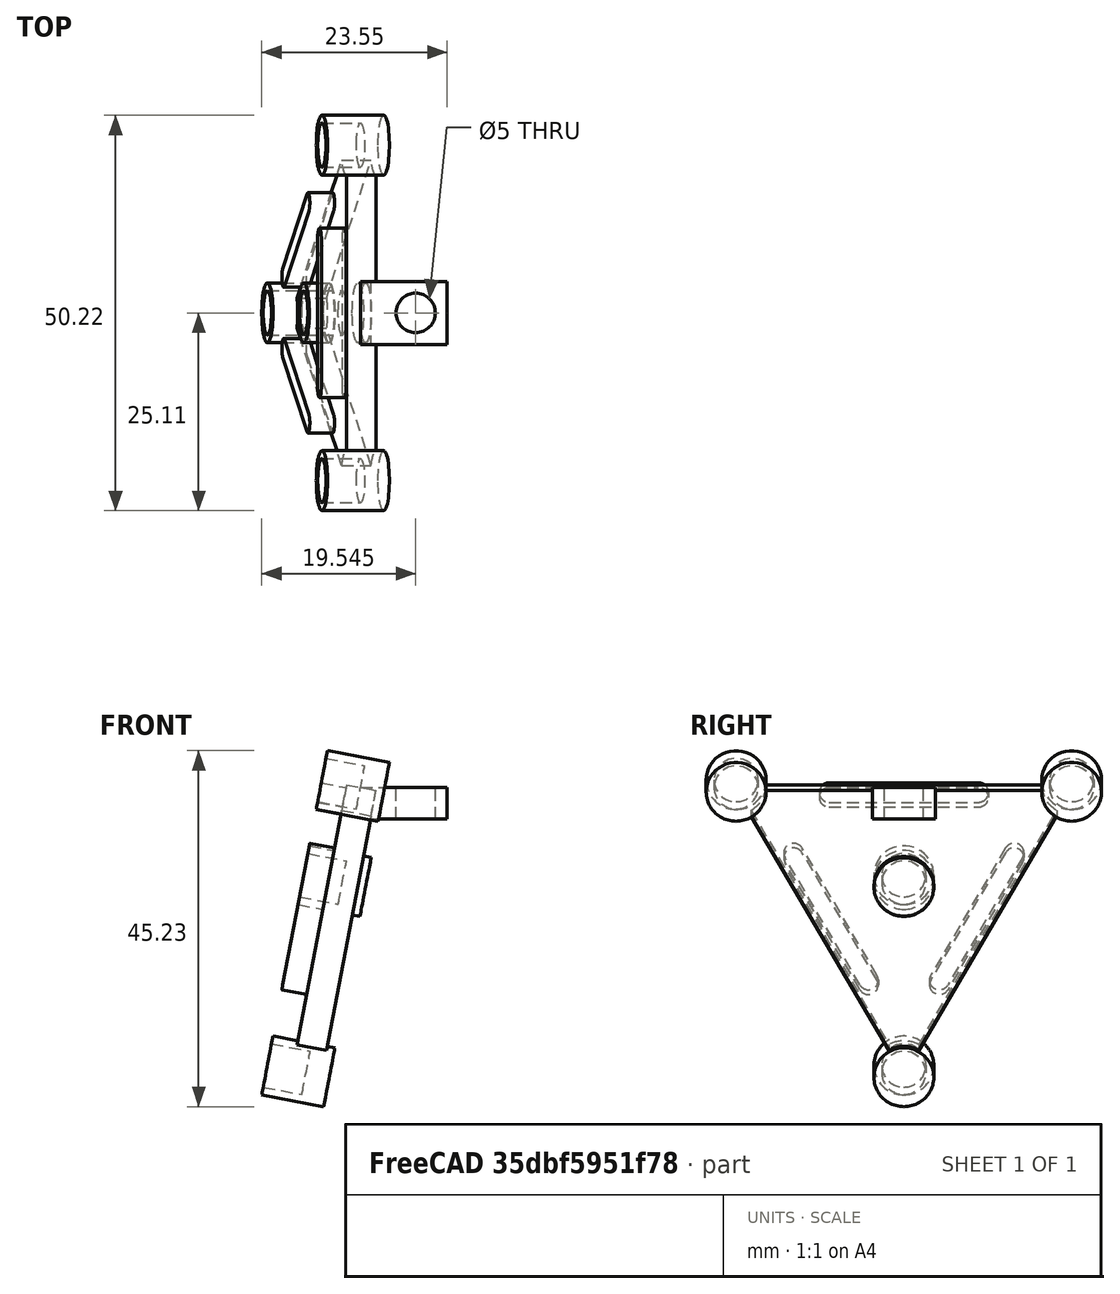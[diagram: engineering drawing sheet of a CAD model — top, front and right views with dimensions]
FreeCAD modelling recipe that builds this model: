
FCSTD DOCUMENT  (FreeCAD 0.19R24267 +99 (Git))
Label: PCB_export
License: All rights reserved
LicenseURL: http://en.wikipedia.org/wiki/All_rights_reserved
objects: Part::Feature×3, Part::Part2DObjectPython×2, Sketcher::SketchObject×2
note: 7 computed .brp shape members not serialized (recipe doc carries the construction recipe); baked Part::Feature solids carry a one-line shape summary decoded from their .brp

FEATURE [Part::Feature] Shape
  Placement = pos=(0,0,0) rot=(0,1,0;0.188711rad)
  shape: bbox 26.49 x 83.96 x 75.99 mm, 229 faces (baked)
FEATURE [Part::Feature] Shape001
  Placement = pos=(0,0,0) rot=(0,1,0;0.188711rad)
  shape: bbox 11.8 x 62.95 x 53.85 mm, 54 faces (baked)
FEATURE [Part::Feature] Shape002
  shape: bbox 23.55 x 50.22 x 45.22 mm, 59 faces (baked)
FEATURE [Part::Part2DObjectPython] Shape2DView  # Draft 2D object (typed FeaturePython)
  Base = -> Shape
  FuseArch = false
  HiddenLines = false
  InPlace = true
  Projection = (0.982247,0,-0.187593)
  ProjectionMode = 0
  SegmentLength = 0.05
  Tessellation = false
  VisibleOnly = false
FEATURE [Part::Part2DObjectPython] Shape2DView001  # Draft 2D object (typed FeaturePython)
  Base = -> Shape001
  FuseArch = false
  HiddenLines = false
  InPlace = true
  Projection = (0.982247,0,-0.187593)
  ProjectionMode = 0
  SegmentLength = 0.05
  Tessellation = false
  VisibleOnly = false
FEATURE [Sketcher::SketchObject] Sketch  label="pcb_all"
  ExternalGeometry = -> [Shape2DView001]
  FullyConstrained = false
  Placement = pos=(0,0,0) rot=(0,0,1;3.14159rad)
  sketch-geometry (323):
    g0: ArcOfEllipse CenterX=-1.99e-14 CenterY=3.45e-14 CenterZ=0 NormalX=0 NormalY=0 NormalZ=1 MajorRadius=76.0845 MinorRadius=27.1486 AngleXU=0.523599 StartAngle=4.15881 EndAngle=5.26596
    g1: ArcOfEllipse CenterX=0 CenterY=0 CenterZ=0 NormalX=0 NormalY=0 NormalZ=1 MajorRadius=76.0845 MinorRadius=27.1486 AngleXU=2.61799 StartAngle=4.15881 EndAngle=5.26596
    g2: ArcOfEllipse CenterX=0 CenterY=0 CenterZ=0 NormalX=0 NormalY=0 NormalZ=1 MajorRadius=76.0845 MinorRadius=27.1486 AngleXU=-1.5708 StartAngle=4.15881 EndAngle=5.26596
    g3: LineSegment StartX=-20.8022 StartY=-36.0305 StartZ=0 EndX=-23.094 EndY=-40 EndZ=0
    g4: LineSegment StartX=41.6044 StartY=-5.68e-14 StartZ=0 EndX=-20.8022 EndY=-36.0305 EndZ=0
    g5: LineSegment StartX=41.6044 StartY=-4.77e-14 StartZ=0 EndX=46.188 EndY=-4.83e-14 EndZ=0
    g6: ArcOfEllipse CenterX=1.78111 CenterY=-28.2981 CenterZ=0 NormalX=0 NormalY=0 NormalZ=1 MajorRadius=2.8 MinorRadius=0.999102 AngleXU=0.523599 StartAngle=3.14159 EndAngle=4.71239
    g7: ArcOfEllipse CenterX=1.78111 CenterY=-28.2981 CenterZ=0 NormalX=0 NormalY=0 NormalZ=1 MajorRadius=2.8 MinorRadius=0.999102 AngleXU=0.523599 StartAngle=0 EndAngle=3.14159
    g8: ArcOfEllipse CenterX=1.78111 CenterY=-28.2981 CenterZ=0 NormalX=0 NormalY=0 NormalZ=1 MajorRadius=2.8 MinorRadius=0.999102 AngleXU=0.523599 StartAngle=4.71239 EndAngle=6.28319
    g9: ArcOfEllipse CenterX=12.8964 CenterY=-22.3371 CenterZ=0 NormalX=0 NormalY=0 NormalZ=1 MajorRadius=2.8 MinorRadius=0.999102 AngleXU=0.523599 StartAngle=3.14159 EndAngle=4.71239
    g10: ArcOfEllipse CenterX=12.8964 CenterY=-22.3371 CenterZ=0 NormalX=0 NormalY=0 NormalZ=1 MajorRadius=2.8 MinorRadius=0.999102 AngleXU=0.523599 StartAngle=1.42745 EndAngle=3.14159
    g11: ArcOfEllipse CenterX=12.8964 CenterY=-22.3371 CenterZ=0 NormalX=0 NormalY=0 NormalZ=1 MajorRadius=2.8 MinorRadius=0.999102 AngleXU=0.523599 StartAngle=0 EndAngle=0.600419
    g12: ArcOfEllipse CenterX=12.8964 CenterY=-22.3371 CenterZ=0 NormalX=0 NormalY=0 NormalZ=1 MajorRadius=2.8 MinorRadius=0.999102 AngleXU=0.523599 StartAngle=4.71239 EndAngle=6.28319
    g13: ArcOfEllipse CenterX=-9.38874 CenterY=-33.3917 CenterZ=0 NormalX=0 NormalY=0 NormalZ=1 MajorRadius=2.8 MinorRadius=0.999102 AngleXU=0.523599 StartAngle=3.14159 EndAngle=4.71239
    g14: ArcOfEllipse CenterX=-9.38874 CenterY=-33.3917 CenterZ=0 NormalX=0 NormalY=0 NormalZ=1 MajorRadius=2.8 MinorRadius=0.999102 AngleXU=0.523599 StartAngle=0 EndAngle=3.14159
    g15: ArcOfEllipse CenterX=-9.38874 CenterY=-33.3917 CenterZ=0 NormalX=0 NormalY=0 NormalZ=1 MajorRadius=2.8 MinorRadius=0.999102 AngleXU=0.523599 StartAngle=4.71239 EndAngle=6.28319
    g16: LineSegment StartX=11.594 StartY=-20.0813 StartZ=0 EndX=12.2184 EndY=-21.1629 EndZ=0
    g17: LineSegment StartX=12.2184 StartY=-21.1629 StartZ=0 EndX=3.55815 EndY=-26.1629 EndZ=0
    g18: LineSegment StartX=2.93371 StartY=-25.0813 StartZ=0 EndX=3.55815 EndY=-26.1629 EndZ=0
    g19: LineSegment StartX=11.594 StartY=-20.0813 StartZ=0 EndX=11.2476 EndY=-20.2813 EndZ=0
    g20: LineSegment StartX=3.28012 StartY=-24.8813 StartZ=0 EndX=2.93371 EndY=-25.0813 EndZ=0
    g21: LineSegment StartX=10.6945 StartY=-19.3234 StartZ=0 EndX=2.72704 EndY=-23.9234 EndZ=0
    g22: LineSegment StartX=10.6945 StartY=-19.3234 StartZ=0 EndX=11.1762 EndY=-20.1577 EndZ=0
    g23: ArcOfEllipse CenterX=23.6163 CenterY=-15.6915 CenterZ=0 NormalX=0 NormalY=0 NormalZ=1 MajorRadius=2.8 MinorRadius=0.999102 AngleXU=0.523599 StartAngle=3.14159 EndAngle=4.71239
    g24: ArcOfEllipse CenterX=23.6163 CenterY=-15.6915 CenterZ=0 NormalX=0 NormalY=0 NormalZ=1 MajorRadius=2.8 MinorRadius=0.999102 AngleXU=0.523599 StartAngle=0 EndAngle=3.14159
    g25: ArcOfEllipse CenterX=23.6163 CenterY=-15.6915 CenterZ=0 NormalX=0 NormalY=0 NormalZ=1 MajorRadius=2.8 MinorRadius=0.999102 AngleXU=0.523599 StartAngle=4.71239 EndAngle=6.28319
    g26: ArcOfEllipse CenterX=33.6124 CenterY=-8.56496 CenterZ=0 NormalX=0 NormalY=0 NormalZ=1 MajorRadius=2.8 MinorRadius=0.999102 AngleXU=0.523599 StartAngle=3.14159 EndAngle=4.71239
    g27: ArcOfEllipse CenterX=33.6124 CenterY=-8.56496 CenterZ=0 NormalX=0 NormalY=0 NormalZ=1 MajorRadius=2.8 MinorRadius=0.999102 AngleXU=0.523599 StartAngle=0 EndAngle=3.14159
    g28: ArcOfEllipse CenterX=33.6124 CenterY=-8.56496 CenterZ=0 NormalX=0 NormalY=0 NormalZ=1 MajorRadius=2.8 MinorRadius=0.999102 AngleXU=0.523599 StartAngle=4.71239 EndAngle=6.28319
    g29: LineSegment StartX=19.9792 StartY=-15.4049 StartZ=0 EndX=12.0117 EndY=-20.0049 EndZ=0
    g30: LineSegment StartX=19.9792 StartY=-15.4049 StartZ=0 EndX=20.4609 EndY=-16.2393 EndZ=0
    g31: LineSegment StartX=10.9695 StartY=-18.9998 StartZ=0 EndX=11.594 EndY=-20.0813 EndZ=0
    g32: LineSegment StartX=19.6298 StartY=-13.9998 StartZ=0 EndX=10.9695 EndY=-18.9998 EndZ=0
    g33: LineSegment StartX=19.6298 StartY=-13.9998 StartZ=0 EndX=20.2542 EndY=-15.0813 EndZ=0
    g34: LineSegment StartX=20.2542 StartY=-15.0813 StartZ=0 EndX=11.594 EndY=-20.0813 EndZ=0
    g35: LineSegment StartX=-20.8022 StartY=36.0305 StartZ=0 EndX=41.6044 EndY=5.68e-14 EndZ=0
    g36: LineSegment StartX=-23.094 StartY=40 StartZ=0 EndX=-20.8022 EndY=36.0305 EndZ=0
    g37: ArcOfEllipse CenterX=33.6124 CenterY=8.56496 CenterZ=0 NormalX=0 NormalY=0 NormalZ=1 MajorRadius=2.8 MinorRadius=0.999102 AngleXU=2.61799 StartAngle=3.14159 EndAngle=4.71239
    g38: ArcOfEllipse CenterX=33.6124 CenterY=8.56496 CenterZ=0 NormalX=0 NormalY=0 NormalZ=1 MajorRadius=2.8 MinorRadius=0.999102 AngleXU=2.61799 StartAngle=-9e-16 EndAngle=3.14159
    g39: ArcOfEllipse CenterX=33.6124 CenterY=8.56496 CenterZ=0 NormalX=0 NormalY=0 NormalZ=1 MajorRadius=2.8 MinorRadius=0.999102 AngleXU=2.61799 StartAngle=4.71239 EndAngle=6.28319
    g40: ArcOfEllipse CenterX=23.6163 CenterY=15.6915 CenterZ=0 NormalX=0 NormalY=0 NormalZ=1 MajorRadius=2.8 MinorRadius=0.999102 AngleXU=2.61799 StartAngle=3.14159 EndAngle=4.71239
    g41: ArcOfEllipse CenterX=23.6163 CenterY=15.6915 CenterZ=0 NormalX=0 NormalY=0 NormalZ=1 MajorRadius=2.8 MinorRadius=0.999102 AngleXU=2.61799 StartAngle=-9e-16 EndAngle=3.14159
    g42: ArcOfEllipse CenterX=23.6163 CenterY=15.6915 CenterZ=0 NormalX=0 NormalY=0 NormalZ=1 MajorRadius=2.8 MinorRadius=0.999102 AngleXU=2.61799 StartAngle=4.71239 EndAngle=6.28319
    g43: LineSegment StartX=11.594 StartY=20.0813 StartZ=0 EndX=12.2184 EndY=21.1629 EndZ=0
    g44: LineSegment StartX=12.2184 StartY=21.1629 StartZ=0 EndX=20.8787 EndY=16.1629 EndZ=0
    g45: LineSegment StartX=20.2542 StartY=15.0813 StartZ=0 EndX=20.8787 EndY=16.1629 EndZ=0
    g46: LineSegment StartX=11.594 StartY=20.0813 StartZ=0 EndX=11.9404 EndY=19.8813 EndZ=0
    g47: LineSegment StartX=19.9078 StartY=15.2813 StartZ=0 EndX=20.2542 EndY=15.0813 EndZ=0
    g48: LineSegment StartX=11.3873 StartY=18.9234 StartZ=0 EndX=19.3547 EndY=14.3234 EndZ=0
    g49: LineSegment StartX=19.3547 StartY=14.3234 StartZ=0 EndX=19.8364 EndY=15.1577 EndZ=0
    g50: ArcOfEllipse CenterX=12.8964 CenterY=22.3371 CenterZ=0 NormalX=0 NormalY=0 NormalZ=1 MajorRadius=2.8 MinorRadius=0.999102 AngleXU=2.61799 StartAngle=3.14159 EndAngle=4.71239
    g51: ArcOfEllipse CenterX=12.8964 CenterY=22.3371 CenterZ=0 NormalX=0 NormalY=0 NormalZ=1 MajorRadius=2.8 MinorRadius=0.999102 AngleXU=2.61799 StartAngle=1.42745 EndAngle=3.14159
    g52: ArcOfEllipse CenterX=12.8964 CenterY=22.3371 CenterZ=0 NormalX=0 NormalY=0 NormalZ=1 MajorRadius=2.8 MinorRadius=0.999102 AngleXU=2.61799 StartAngle=-9e-16 EndAngle=0.600419
    g53: ArcOfEllipse CenterX=12.8964 CenterY=22.3371 CenterZ=0 NormalX=0 NormalY=0 NormalZ=1 MajorRadius=2.8 MinorRadius=0.999102 AngleXU=2.61799 StartAngle=4.71239 EndAngle=6.28319
    g54: ArcOfEllipse CenterX=1.78111 CenterY=28.2981 CenterZ=0 NormalX=0 NormalY=0 NormalZ=1 MajorRadius=2.8 MinorRadius=0.999102 AngleXU=2.61799 StartAngle=3.14159 EndAngle=4.71239
    g55: ArcOfEllipse CenterX=1.78111 CenterY=28.2981 CenterZ=0 NormalX=0 NormalY=0 NormalZ=1 MajorRadius=2.8 MinorRadius=0.999102 AngleXU=2.61799 StartAngle=-9e-16 EndAngle=3.14159
    g56: ArcOfEllipse CenterX=1.78111 CenterY=28.2981 CenterZ=0 NormalX=0 NormalY=0 NormalZ=1 MajorRadius=2.8 MinorRadius=0.999102 AngleXU=2.61799 StartAngle=4.71239 EndAngle=6.28319
    g57: LineSegment StartX=3.35148 StartY=25.0049 StartZ=0 EndX=11.3189 EndY=20.4049 EndZ=0
    g58: LineSegment StartX=11.3189 StartY=20.4049 StartZ=0 EndX=11.8006 EndY=21.2393 EndZ=0
    g59: LineSegment StartX=10.9695 StartY=18.9998 StartZ=0 EndX=11.594 EndY=20.0813 EndZ=0
    g60: LineSegment StartX=2.30927 StartY=23.9998 StartZ=0 EndX=10.9695 EndY=18.9998 EndZ=0
    g61: LineSegment StartX=2.30927 StartY=23.9998 StartZ=0 EndX=2.93371 EndY=25.0813 EndZ=0
    g62: LineSegment StartX=2.93371 StartY=25.0813 StartZ=0 EndX=11.594 EndY=20.0813 EndZ=0
    g63: ArcOfEllipse CenterX=-9.38874 CenterY=33.3917 CenterZ=0 NormalX=0 NormalY=0 NormalZ=1 MajorRadius=2.8 MinorRadius=0.999102 AngleXU=2.61799 StartAngle=3.14159 EndAngle=4.71239
    g64: ArcOfEllipse CenterX=-9.38874 CenterY=33.3917 CenterZ=0 NormalX=0 NormalY=0 NormalZ=1 MajorRadius=2.8 MinorRadius=0.999102 AngleXU=2.61799 StartAngle=-9e-16 EndAngle=3.14159
    g65: ArcOfEllipse CenterX=-9.38874 CenterY=33.3917 CenterZ=0 NormalX=0 NormalY=0 NormalZ=1 MajorRadius=2.8 MinorRadius=0.999102 AngleXU=2.61799 StartAngle=4.71239 EndAngle=6.28319
    g66: LineSegment StartX=-20.8022 StartY=-36.0305 StartZ=0 EndX=-20.8022 EndY=36.0305 EndZ=0
    g67: ArcOfEllipse CenterX=-24.2237 CenterY=-24.8267 CenterZ=0 NormalX=0 NormalY=0 NormalZ=1 MajorRadius=2.8 MinorRadius=0.999102 AngleXU=-1.5708 StartAngle=3.14159 EndAngle=4.71239
    g68: ArcOfEllipse CenterX=-24.2237 CenterY=-24.8267 CenterZ=0 NormalX=0 NormalY=0 NormalZ=1 MajorRadius=2.8 MinorRadius=0.999102 AngleXU=-1.5708 StartAngle=0 EndAngle=3.14159
    g69: ArcOfEllipse CenterX=-24.2237 CenterY=-24.8267 CenterZ=0 NormalX=0 NormalY=0 NormalZ=1 MajorRadius=2.8 MinorRadius=0.999102 AngleXU=-1.5708 StartAngle=4.71239 EndAngle=6.28319
    g70: LineSegment StartX=-21.939 StartY=-10 StartZ=0 EndX=-21.939 EndY=-3.6e-15 EndZ=0
    g71: LineSegment StartX=-21.939 StartY=-10 StartZ=0 EndX=-23.1879 EndY=-10 EndZ=0
    g72: LineSegment StartX=-23.1879 StartY=-10 StartZ=0 EndX=-23.1879 EndY=-3.6e-15 EndZ=0
    g73: LineSegment StartX=-21.939 StartY=-6.2e-15 StartZ=0 EndX=-23.1879 EndY=-6e-15 EndZ=0
    g74: LineSegment StartX=-23.3306 StartY=-9.6 StartZ=0 EndX=-23.3306 EndY=-0.4 EndZ=0
    g75: ArcOfEllipse CenterX=-25.3974 CenterY=-12.6066 CenterZ=0 NormalX=0 NormalY=0 NormalZ=1 MajorRadius=2.8 MinorRadius=0.999102 AngleXU=-1.5708 StartAngle=3.14159 EndAngle=4.71239
    g76: ArcOfEllipse CenterX=-25.3974 CenterY=-12.6066 CenterZ=0 NormalX=0 NormalY=0 NormalZ=1 MajorRadius=2.8 MinorRadius=0.999102 AngleXU=-1.5708 StartAngle=0 EndAngle=3.14159
    g77: ArcOfEllipse CenterX=-25.3974 CenterY=-12.6066 CenterZ=0 NormalX=0 NormalY=0 NormalZ=1 MajorRadius=2.8 MinorRadius=0.999102 AngleXU=-1.5708 StartAngle=4.71239 EndAngle=6.28319
    g78: LineSegment StartX=-22.0818 StartY=0.4 StartZ=0 EndX=-22.0818 EndY=9.6 EndZ=0
    g79: LineSegment StartX=-23.1879 StartY=-5.4e-15 StartZ=0 EndX=-24.4368 EndY=-5.2e-15 EndZ=0
    g80: LineSegment StartX=-24.4368 StartY=-5.2e-15 StartZ=0 EndX=-24.4368 EndY=10 EndZ=0
    g81: LineSegment StartX=-23.1879 StartY=10 StartZ=0 EndX=-24.4368 EndY=10 EndZ=0
    g82: LineSegment StartX=-23.1879 StartY=-5.4e-15 StartZ=0 EndX=-23.1879 EndY=0.4 EndZ=0
    g83: LineSegment StartX=-23.1879 StartY=9.6 StartZ=0 EndX=-23.1879 EndY=10 EndZ=0
    g84: ArcOfEllipse CenterX=-24.2237 CenterY=24.8267 CenterZ=0 NormalX=0 NormalY=0 NormalZ=1 MajorRadius=2.8 MinorRadius=0.999102 AngleXU=-1.5708 StartAngle=3.14159 EndAngle=4.71239
    g85: ArcOfEllipse CenterX=-24.2237 CenterY=24.8267 CenterZ=0 NormalX=0 NormalY=0 NormalZ=1 MajorRadius=2.8 MinorRadius=0.999102 AngleXU=-1.5708 StartAngle=0 EndAngle=3.14159
    g86: ArcOfEllipse CenterX=-24.2237 CenterY=24.8267 CenterZ=0 NormalX=0 NormalY=0 NormalZ=1 MajorRadius=2.8 MinorRadius=0.999102 AngleXU=-1.5708 StartAngle=4.71239 EndAngle=6.28319
    g87: ArcOfEllipse CenterX=-25.3974 CenterY=12.6066 CenterZ=0 NormalX=0 NormalY=0 NormalZ=1 MajorRadius=2.8 MinorRadius=0.999102 AngleXU=-1.5708 StartAngle=3.14159 EndAngle=4.71239
    g88: ArcOfEllipse CenterX=-25.3974 CenterY=12.6066 CenterZ=0 NormalX=0 NormalY=0 NormalZ=1 MajorRadius=2.8 MinorRadius=0.999102 AngleXU=-1.5708 StartAngle=0 EndAngle=3.14159
    g89: ArcOfEllipse CenterX=-25.3974 CenterY=12.6066 CenterZ=0 NormalX=0 NormalY=0 NormalZ=1 MajorRadius=2.8 MinorRadius=0.999102 AngleXU=-1.5708 StartAngle=4.71239 EndAngle=6.28319
    g90: ArcOfEllipse CenterX=-25.7927 CenterY=-5.7e-15 CenterZ=0 NormalX=0 NormalY=0 NormalZ=1 MajorRadius=2.8 MinorRadius=0.999102 AngleXU=-1.5708 StartAngle=3.14159 EndAngle=4.71239
    g91: ArcOfEllipse CenterX=-25.7927 CenterY=-5.7e-15 CenterZ=0 NormalX=0 NormalY=0 NormalZ=1 MajorRadius=2.8 MinorRadius=0.999102 AngleXU=-1.5708 StartAngle=1.42745 EndAngle=3.14159
    g92: ArcOfEllipse CenterX=-25.7927 CenterY=-5.7e-15 CenterZ=0 NormalX=0 NormalY=0 NormalZ=1 MajorRadius=2.8 MinorRadius=0.999102 AngleXU=-1.5708 StartAngle=0 EndAngle=0.600418
    g93: ArcOfEllipse CenterX=-25.7927 CenterY=-5.7e-15 CenterZ=0 NormalX=0 NormalY=0 NormalZ=1 MajorRadius=2.8 MinorRadius=0.999102 AngleXU=-1.5708 StartAngle=4.71239 EndAngle=6.28319
    g94: LineSegment StartX=31.5162 StartY=2.7 StartZ=0 EndX=31.5162 EndY=-2.7 EndZ=0
    g95: LineSegment StartX=31.5162 StartY=2.7 StartZ=0 EndX=28.66 EndY=2.7 EndZ=0
    g96: LineSegment StartX=31.5162 StartY=-2.7 StartZ=0 EndX=28.66 EndY=-2.7 EndZ=0
    g97: LineSegment StartX=28.66 StartY=2.7 StartZ=0 EndX=28.66 EndY=-2.7 EndZ=0
    g98: LineSegment StartX=22.2288 StartY=-3.08496 StartZ=0 EndX=21.4166 EndY=-8.4281 EndZ=0
    g99: LineSegment StartX=22.2288 StartY=-3.08496 StartZ=0 EndX=19.5842 EndY=-2.64282 EndZ=0
    g100: LineSegment StartX=21.4166 StartY=-8.4281 StartZ=0 EndX=18.7719 EndY=-7.98597 EndZ=0
    g101: LineSegment StartX=19.5842 StartY=-2.64282 StartZ=0 EndX=18.7719 EndY=-7.98597 EndZ=0
    g102: Ellipse CenterX=24.6094 CenterY=-1.48e-14 CenterZ=0 NormalX=0 NormalY=0 NormalZ=-1 MajorRadius=2.8 MinorRadius=2.8 AngleXU=-1.5708
    g103: LineSegment StartX=14.453 StartY=-9.27479 StartZ=0 EndX=11.1035 EndY=-13.5115 EndZ=0
    g104: LineSegment StartX=14.453 StartY=-9.27479 StartZ=0 EndX=12.4191 EndY=-7.6504 EndZ=0
    g105: LineSegment StartX=11.1035 StartY=-13.5115 StartZ=0 EndX=9.0696 EndY=-11.8871 EndZ=0
    g106: LineSegment StartX=12.4191 StartY=-7.6504 StartZ=0 EndX=9.0696 EndY=-11.8871 EndZ=0
    g107: LineSegment StartX=13.0401 StartY=2.7 StartZ=0 EndX=13.0401 EndY=-2.7 EndZ=0
    g108: LineSegment StartX=13.0401 StartY=2.7 StartZ=0 EndX=10.4825 EndY=2.7 EndZ=0
    g109: LineSegment StartX=13.0401 StartY=-2.7 StartZ=0 EndX=10.4825 EndY=-2.7 EndZ=0
    g110: LineSegment StartX=10.4825 StartY=2.7 StartZ=0 EndX=10.4825 EndY=-2.7 EndZ=0
    g111: LineSegment StartX=6.24058 StartY=-15.9088 StartZ=0 EndX=1.08812 EndY=-17.5314 EndZ=0
    g112: LineSegment StartX=6.24058 StartY=-15.9088 StartZ=0 EndX=5.47732 EndY=-13.4207 EndZ=0
    g113: LineSegment StartX=1.08812 StartY=-17.5314 StartZ=0 EndX=0.324852 EndY=-15.0434 EndZ=0
    g114: LineSegment StartX=5.47732 StartY=-13.4207 StartZ=0 EndX=0.324852 EndY=-15.0434 EndZ=0
    g115: LineSegment StartX=-7.65131 StartY=-18.4458 StartZ=0 EndX=-2.48785 EndY=-20.0282 EndZ=0
    g116: LineSegment StartX=-7.65131 StartY=-18.4458 StartZ=0 EndX=-8.4248 EndY=-21.015 EndZ=0
    g117: LineSegment StartX=-2.48785 StartY=-20.0282 StartZ=0 EndX=-3.26134 EndY=-22.5974 EndZ=0
    g118: LineSegment StartX=-8.4248 StartY=-21.015 StartZ=0 EndX=-3.26134 EndY=-22.5974 EndZ=0
    g119: LineSegment StartX=-16.6086 StartY=-23.4248 StartZ=0 EndX=-12.0029 EndY=-26.2446 EndZ=0
    g120: LineSegment StartX=-16.6086 StartY=-23.4248 StartZ=0 EndX=-18.0852 EndY=-25.8694 EndZ=0
    g121: LineSegment StartX=-12.0029 StartY=-26.2446 StartZ=0 EndX=-13.4794 EndY=-28.6893 EndZ=0
    g122: LineSegment StartX=-18.0852 StartY=-25.8694 StartZ=0 EndX=-13.4794 EndY=-28.6893 EndZ=0
    g123: Ellipse CenterX=-12.3047 CenterY=-21.3123 CenterZ=0 NormalX=0 NormalY=0 NormalZ=-1 MajorRadius=2.8 MinorRadius=2.8 AngleXU=-1.5708
    g124: LineSegment StartX=-15.9324 StartY=-12.1009 StartZ=0 EndX=-12.2152 EndY=-16.0181 EndZ=0
    g125: LineSegment StartX=-15.9324 StartY=-12.1009 StartZ=0 EndX=-17.8729 EndY=-13.9541 EndZ=0
    g126: LineSegment StartX=-12.2152 StartY=-16.0181 StartZ=0 EndX=-14.1557 EndY=-17.8713 EndZ=0
    g127: LineSegment StartX=-17.8729 StartY=-13.9541 StartZ=0 EndX=-14.1557 EndY=-17.8713 EndZ=0
    g128: LineSegment StartX=-7.09411 StartY=-7.42317 StartZ=0 EndX=-2.48907 EndY=-10.2439 EndZ=0
    g129: LineSegment StartX=-7.09411 StartY=-7.42317 StartZ=0 EndX=-8.42358 EndY=-9.60312 EndZ=0
    g130: LineSegment StartX=-2.48907 StartY=-10.2439 StartZ=0 EndX=-3.81854 EndY=-12.4238 EndZ=0
    g131: LineSegment StartX=-8.42358 StartY=-9.60312 StartZ=0 EndX=-3.81854 EndY=-12.4238 EndZ=0
    g132: LineSegment StartX=6.20634 StartY=-4.47515 StartZ=0 EndX=1.83387 EndY=-7.64413 EndZ=0
    g133: LineSegment StartX=6.20634 StartY=-4.47515 StartZ=0 EndX=4.73157 EndY=-2.43773 EndZ=0
    g134: LineSegment StartX=1.83387 StartY=-7.64413 StartZ=0 EndX=0.359097 EndY=-5.6067 EndZ=0
    g135: LineSegment StartX=4.73157 StartY=-2.43773 StartZ=0 EndX=0.359097 EndY=-5.6067 EndZ=0
    g136: Ellipse CenterX=4.23297e-06 CenterY=-4.6e-15 CenterZ=0 NormalX=0 NormalY=0 NormalZ=-1 MajorRadius=2.8 MinorRadius=2.8 AngleXU=-1.5708
    g137: LineSegment StartX=-4.20007 StartY=2.7 StartZ=0 EndX=-4.20007 EndY=-2.7 EndZ=0
    g138: LineSegment StartX=-4.20007 StartY=2.7 StartZ=0 EndX=-6.71258 EndY=2.7 EndZ=0
    g139: LineSegment StartX=-4.20007 StartY=-2.7 StartZ=0 EndX=-6.71258 EndY=-2.7 EndZ=0
    g140: LineSegment StartX=-6.71258 StartY=2.7 StartZ=0 EndX=-6.71258 EndY=-2.7 EndZ=0
    g141: LineSegment StartX=-14.6048 StartY=-1.92893 StartZ=0 EndX=-12.9986 EndY=-7.08455 EndZ=0
    g142: LineSegment StartX=-14.6048 StartY=-1.92893 StartZ=0 EndX=-17.0895 EndY=-2.7057 EndZ=0
    g143: LineSegment StartX=-12.9986 StartY=-7.08455 StartZ=0 EndX=-15.4833 EndY=-7.86133 EndZ=0
    g144: LineSegment StartX=-17.0895 StartY=-2.7057 StartZ=0 EndX=-15.4833 EndY=-7.86133 EndZ=0
    g145: LineSegment StartX=21.4166 StartY=8.4281 StartZ=0 EndX=22.2288 EndY=3.08496 EndZ=0
    g146: LineSegment StartX=21.4166 StartY=8.4281 StartZ=0 EndX=18.7719 EndY=7.98597 EndZ=0
    g147: LineSegment StartX=22.2288 StartY=3.08496 StartZ=0 EndX=19.5842 EndY=2.64282 EndZ=0
    g148: LineSegment StartX=18.7719 StartY=7.98597 StartZ=0 EndX=19.5842 EndY=2.64282 EndZ=0
    g149: LineSegment StartX=11.1035 StartY=13.5115 StartZ=0 EndX=14.453 EndY=9.27479 EndZ=0
    g150: LineSegment StartX=11.1035 StartY=13.5115 StartZ=0 EndX=9.0696 EndY=11.8871 EndZ=0
    g151: LineSegment StartX=14.453 StartY=9.27479 StartZ=0 EndX=12.4191 EndY=7.6504 EndZ=0
    g152: LineSegment StartX=9.0696 StartY=11.8871 StartZ=0 EndX=12.4191 EndY=7.6504 EndZ=0
    g153: LineSegment StartX=1.83387 StartY=7.64413 StartZ=0 EndX=6.20634 EndY=4.47515 EndZ=0
    g154: LineSegment StartX=1.83387 StartY=7.64413 StartZ=0 EndX=0.359097 EndY=5.6067 EndZ=0
    g155: LineSegment StartX=6.20634 StartY=4.47515 StartZ=0 EndX=4.73157 EndY=2.43773 EndZ=0
    g156: LineSegment StartX=0.359097 StartY=5.6067 StartZ=0 EndX=4.73157 EndY=2.43773 EndZ=0
    g157: LineSegment StartX=-2.48907 StartY=10.2439 StartZ=0 EndX=-7.09411 EndY=7.42317 EndZ=0
    g158: LineSegment StartX=-2.48907 StartY=10.2439 StartZ=0 EndX=-3.81854 EndY=12.4238 EndZ=0
    g159: LineSegment StartX=-7.09411 StartY=7.42317 StartZ=0 EndX=-8.42358 EndY=9.60312 EndZ=0
    g160: LineSegment StartX=-3.81854 StartY=12.4238 StartZ=0 EndX=-8.42358 EndY=9.60312 EndZ=0
    g161: LineSegment StartX=-12.9986 StartY=7.08455 StartZ=0 EndX=-14.6048 EndY=1.92893 EndZ=0
    g162: LineSegment StartX=-12.9986 StartY=7.08455 StartZ=0 EndX=-15.4833 EndY=7.86133 EndZ=0
    g163: LineSegment StartX=-14.6048 StartY=1.92893 StartZ=0 EndX=-17.0895 EndY=2.7057 EndZ=0
    g164: LineSegment StartX=-15.4833 StartY=7.86133 StartZ=0 EndX=-17.0895 EndY=2.7057 EndZ=0
    g165: LineSegment StartX=1.08812 StartY=17.5314 StartZ=0 EndX=6.24058 EndY=15.9088 EndZ=0
    g166: LineSegment StartX=1.08812 StartY=17.5314 StartZ=0 EndX=0.324852 EndY=15.0434 EndZ=0
    g167: LineSegment StartX=6.24058 StartY=15.9088 StartZ=0 EndX=5.47732 EndY=13.4207 EndZ=0
    g168: LineSegment StartX=0.324852 StartY=15.0434 StartZ=0 EndX=5.47732 EndY=13.4207 EndZ=0
    g169: LineSegment StartX=-2.48785 StartY=20.0282 StartZ=0 EndX=-7.65131 EndY=18.4458 EndZ=0
    g170: LineSegment StartX=-2.48785 StartY=20.0282 StartZ=0 EndX=-3.26134 EndY=22.5974 EndZ=0
    g171: LineSegment StartX=-7.65131 StartY=18.4458 StartZ=0 EndX=-8.4248 EndY=21.015 EndZ=0
    g172: LineSegment StartX=-3.26134 StartY=22.5974 StartZ=0 EndX=-8.4248 EndY=21.015 EndZ=0
    g173: LineSegment StartX=-12.2152 StartY=16.0181 StartZ=0 EndX=-15.9324 EndY=12.1009 EndZ=0
    g174: LineSegment StartX=-12.2152 StartY=16.0181 StartZ=0 EndX=-14.1557 EndY=17.8713 EndZ=0
    g175: LineSegment StartX=-15.9324 StartY=12.1009 StartZ=0 EndX=-17.8729 EndY=13.9541 EndZ=0
    g176: LineSegment StartX=-14.1557 StartY=17.8713 StartZ=0 EndX=-17.8729 EndY=13.9541 EndZ=0
    g177: Ellipse CenterX=-12.3047 CenterY=21.3123 CenterZ=0 NormalX=0 NormalY=0 NormalZ=-1 MajorRadius=2.8 MinorRadius=2.8 AngleXU=-1.5708
    g178: LineSegment StartX=-12.0029 StartY=26.2446 StartZ=0 EndX=-16.6086 EndY=23.4248 EndZ=0
    g179: LineSegment StartX=-12.0029 StartY=26.2446 StartZ=0 EndX=-13.4794 EndY=28.6893 EndZ=0
    g180: LineSegment StartX=-16.6086 StartY=23.4248 StartZ=0 EndX=-18.0852 EndY=25.8694 EndZ=0
    g181: LineSegment StartX=-13.4794 StartY=28.6893 StartZ=0 EndX=-18.0852 EndY=25.8694 EndZ=0
    g182: ArcOfEllipse CenterX=0.846934 CenterY=-26.6801 CenterZ=0 NormalX=0 NormalY=0 NormalZ=1 MajorRadius=2.8 MinorRadius=0.999102 AngleXU=0.523599 StartAngle=4.34989 EndAngle=4.71239
    g183: ArcOfEllipse CenterX=0.846934 CenterY=-26.6801 CenterZ=0 NormalX=0 NormalY=0 NormalZ=1 MajorRadius=2.8 MinorRadius=0.999102 AngleXU=0.523599 StartAngle=4.71239 EndAngle=5.07489
    g184: ArcOfEllipse CenterX=11.9622 CenterY=-20.7191 CenterZ=0 NormalX=0 NormalY=0 NormalZ=1 MajorRadius=2.8 MinorRadius=0.999102 AngleXU=0.523599 StartAngle=4.34989 EndAngle=4.71239
    g185: ArcOfEllipse CenterX=11.9622 CenterY=-20.7191 CenterZ=0 NormalX=0 NormalY=0 NormalZ=1 MajorRadius=2.8 MinorRadius=0.999102 AngleXU=0.523599 StartAngle=4.71239 EndAngle=4.85574
    g186: ArcOfEllipse CenterX=-10.3229 CenterY=-31.7737 CenterZ=0 NormalX=0 NormalY=0 NormalZ=1 MajorRadius=2.8 MinorRadius=0.999102 AngleXU=0.523599 StartAngle=4.34989 EndAngle=4.71239
    g187: ArcOfEllipse CenterX=-10.3229 CenterY=-31.7737 CenterZ=0 NormalX=0 NormalY=0 NormalZ=1 MajorRadius=2.8 MinorRadius=0.999102 AngleXU=0.523599 StartAngle=4.71239 EndAngle=5.07489
    g188: LineSegment StartX=11.594 StartY=-20.0813 StartZ=0 EndX=11.1269 EndY=-19.2723 EndZ=0
    g189: LineSegment StartX=11.7513 StartY=-20.3539 StartZ=0 EndX=11.4049 EndY=-20.5539 EndZ=0
    g190: LineSegment StartX=3.43747 StartY=-25.1539 StartZ=0 EndX=3.09106 EndY=-25.3539 EndZ=0
    g191: LineSegment StartX=3.55815 StartY=-26.1629 StartZ=0 EndX=3.09106 EndY=-25.3539 EndZ=0
    g192: LineSegment StartX=2.93371 StartY=-25.0813 StartZ=0 EndX=3.09106 EndY=-25.3539 EndZ=0
    g193: LineSegment StartX=11.1616 StartY=-20.1324 StartZ=0 EndX=10.6945 EndY=-19.3234 EndZ=0
    g194: LineSegment StartX=3.19413 StartY=-24.7324 StartZ=0 EndX=2.72704 EndY=-23.9234 EndZ=0
    g195: LineSegment StartX=11.1616 StartY=-20.1324 StartZ=0 EndX=3.19413 EndY=-24.7324 EndZ=0
    g196: LineSegment StartX=11.1616 StartY=-20.1324 StartZ=0 EndX=11.6433 EndY=-20.9667 EndZ=0
    g197: LineSegment StartX=11.6433 StartY=-20.9667 StartZ=0 EndX=3.67584 EndY=-25.5667 EndZ=0
    g198: LineSegment StartX=3.19413 StartY=-24.7324 StartZ=0 EndX=3.67584 EndY=-25.5667 EndZ=0
    g199: ArcOfEllipse CenterX=22.6822 CenterY=-14.0735 CenterZ=0 NormalX=0 NormalY=0 NormalZ=1 MajorRadius=2.8 MinorRadius=0.999102 AngleXU=0.523599 StartAngle=4.34989 EndAngle=4.71239
    g200: ArcOfEllipse CenterX=22.6822 CenterY=-14.0735 CenterZ=0 NormalX=0 NormalY=0 NormalZ=1 MajorRadius=2.8 MinorRadius=0.999102 AngleXU=0.523599 StartAngle=4.71239 EndAngle=5.07489
    g201: ArcOfEllipse CenterX=32.6783 CenterY=-6.94692 CenterZ=0 NormalX=0 NormalY=0 NormalZ=1 MajorRadius=2.8 MinorRadius=0.999102 AngleXU=0.523599 StartAngle=4.34989 EndAngle=4.71239
    g202: ArcOfEllipse CenterX=32.6783 CenterY=-6.94692 CenterZ=0 NormalX=0 NormalY=0 NormalZ=1 MajorRadius=2.8 MinorRadius=0.999102 AngleXU=0.523599 StartAngle=4.71239 EndAngle=5.07489
    g203: LineSegment StartX=20.4463 StartY=-16.2139 StartZ=0 EndX=19.9792 EndY=-15.4049 EndZ=0
    g204: LineSegment StartX=12.4788 StartY=-20.8139 StartZ=0 EndX=12.0117 EndY=-20.0049 EndZ=0
    g205: LineSegment StartX=20.4463 StartY=-16.2139 StartZ=0 EndX=12.4788 EndY=-20.8139 EndZ=0
    g206: LineSegment StartX=12.4788 StartY=-20.8139 StartZ=0 EndX=12.9605 EndY=-21.6483 EndZ=0
    g207: LineSegment StartX=20.4463 StartY=-16.2139 StartZ=0 EndX=20.928 EndY=-17.0483 EndZ=0
    g208: LineSegment StartX=20.928 StartY=-17.0483 StartZ=0 EndX=12.9605 EndY=-21.6483 EndZ=0
    g209: LineSegment StartX=10.9695 StartY=-18.9998 StartZ=0 EndX=11.1269 EndY=-19.2723 EndZ=0
    g210: LineSegment StartX=19.7871 StartY=-14.2723 StartZ=0 EndX=11.1269 EndY=-19.2723 EndZ=0
    g211: ArcOfEllipse CenterX=32.6783 CenterY=6.94692 CenterZ=0 NormalX=0 NormalY=0 NormalZ=1 MajorRadius=2.8 MinorRadius=0.999102 AngleXU=2.61799 StartAngle=4.34989 EndAngle=4.71239
    g212: ArcOfEllipse CenterX=32.6783 CenterY=6.94692 CenterZ=0 NormalX=0 NormalY=0 NormalZ=1 MajorRadius=2.8 MinorRadius=0.999102 AngleXU=2.61799 StartAngle=4.71239 EndAngle=5.07489
    g213: ArcOfEllipse CenterX=22.6822 CenterY=14.0735 CenterZ=0 NormalX=0 NormalY=0 NormalZ=1 MajorRadius=2.8 MinorRadius=0.999102 AngleXU=2.61799 StartAngle=4.34989 EndAngle=4.71239
    g214: ArcOfEllipse CenterX=22.6822 CenterY=14.0735 CenterZ=0 NormalX=0 NormalY=0 NormalZ=1 MajorRadius=2.8 MinorRadius=0.999102 AngleXU=2.61799 StartAngle=4.71239 EndAngle=5.07489
    g215: LineSegment StartX=12.2184 StartY=21.1629 StartZ=0 EndX=11.7513 EndY=20.3539 EndZ=0
    g216: LineSegment StartX=11.594 StartY=20.0813 StartZ=0 EndX=11.7513 EndY=20.3539 EndZ=0
    g217: LineSegment StartX=11.7513 StartY=20.3539 StartZ=0 EndX=12.0977 EndY=20.1539 EndZ=0
    g218: LineSegment StartX=20.0652 StartY=15.5539 StartZ=0 EndX=20.4116 EndY=15.3539 EndZ=0
    g219: LineSegment StartX=11.8544 StartY=19.7324 StartZ=0 EndX=11.3873 EndY=18.9234 EndZ=0
    g220: LineSegment StartX=19.8218 StartY=15.1324 StartZ=0 EndX=19.3547 EndY=14.3234 EndZ=0
    g221: LineSegment StartX=11.8544 StartY=19.7324 StartZ=0 EndX=19.8218 EndY=15.1324 EndZ=0
    g222: LineSegment StartX=11.8544 StartY=19.7324 StartZ=0 EndX=12.3361 EndY=20.5667 EndZ=0
    g223: LineSegment StartX=12.3361 StartY=20.5667 StartZ=0 EndX=20.3035 EndY=15.9667 EndZ=0
    g224: LineSegment StartX=19.8218 StartY=15.1324 StartZ=0 EndX=20.3035 EndY=15.9667 EndZ=0
    g225: ArcOfEllipse CenterX=11.9622 CenterY=20.7191 CenterZ=0 NormalX=0 NormalY=0 NormalZ=1 MajorRadius=2.8 MinorRadius=0.999102 AngleXU=2.61799 StartAngle=4.34989 EndAngle=4.71239
    g226: ArcOfEllipse CenterX=11.9622 CenterY=20.7191 CenterZ=0 NormalX=0 NormalY=0 NormalZ=1 MajorRadius=2.8 MinorRadius=0.999102 AngleXU=2.61799 StartAngle=4.71239 EndAngle=4.85574
    g227: ArcOfEllipse CenterX=0.846934 CenterY=26.6801 CenterZ=0 NormalX=0 NormalY=0 NormalZ=1 MajorRadius=2.8 MinorRadius=0.999102 AngleXU=2.61799 StartAngle=4.34989 EndAngle=4.71239
    g228: ArcOfEllipse CenterX=0.846934 CenterY=26.6801 CenterZ=0 NormalX=0 NormalY=0 NormalZ=1 MajorRadius=2.8 MinorRadius=0.999102 AngleXU=2.61799 StartAngle=4.71239 EndAngle=5.07489
    g229: LineSegment StartX=3.81857 StartY=25.8139 StartZ=0 EndX=3.35148 EndY=25.0049 EndZ=0
    g230: LineSegment StartX=11.786 StartY=21.2139 StartZ=0 EndX=11.3189 EndY=20.4049 EndZ=0
    g231: LineSegment StartX=3.81857 StartY=25.8139 StartZ=0 EndX=11.786 EndY=21.2139 EndZ=0
    g232: LineSegment StartX=11.786 StartY=21.2139 StartZ=0 EndX=12.2677 EndY=22.0483 EndZ=0
    g233: LineSegment StartX=3.81857 StartY=25.8139 StartZ=0 EndX=4.30028 EndY=26.6483 EndZ=0
    g234: LineSegment StartX=4.30028 StartY=26.6483 StartZ=0 EndX=12.2677 EndY=22.0483 EndZ=0
    g235: LineSegment StartX=2.93371 StartY=25.0813 StartZ=0 EndX=2.46662 EndY=24.2723 EndZ=0
    g236: LineSegment StartX=2.30927 StartY=23.9998 StartZ=0 EndX=2.46662 EndY=24.2723 EndZ=0
    g237: LineSegment StartX=2.46662 StartY=24.2723 StartZ=0 EndX=11.1269 EndY=19.2723 EndZ=0
    g238: ArcOfEllipse CenterX=-10.3229 CenterY=31.7737 CenterZ=0 NormalX=0 NormalY=0 NormalZ=1 MajorRadius=2.8 MinorRadius=0.999102 AngleXU=2.61799 StartAngle=4.34989 EndAngle=4.71239
    g239: ArcOfEllipse CenterX=-10.3229 CenterY=31.7737 CenterZ=0 NormalX=0 NormalY=0 NormalZ=1 MajorRadius=2.8 MinorRadius=0.999102 AngleXU=2.61799 StartAngle=4.71239 EndAngle=5.07489
    g240: ArcOfEllipse CenterX=-22.3553 CenterY=-24.8267 CenterZ=0 NormalX=0 NormalY=0 NormalZ=1 MajorRadius=2.8 MinorRadius=0.999102 AngleXU=-1.5708 StartAngle=4.34989 EndAngle=4.71239
    g241: ArcOfEllipse CenterX=-22.3553 CenterY=-24.8267 CenterZ=0 NormalX=0 NormalY=0 NormalZ=1 MajorRadius=2.8 MinorRadius=0.999102 AngleXU=-1.5708 StartAngle=4.71239 EndAngle=5.07489
    g242: LineSegment StartX=-21.939 StartY=-10 StartZ=0 EndX=-22.2537 EndY=-10 EndZ=0
    g243: LineSegment StartX=-22.2537 StartY=-10 StartZ=0 EndX=-22.2537 EndY=-3.6e-15 EndZ=0
    g244: LineSegment StartX=-21.939 StartY=-6.2e-15 StartZ=0 EndX=-22.2537 EndY=-6.2e-15 EndZ=0
    g245: LineSegment StartX=-24.2648 StartY=-9.6 StartZ=0 EndX=-23.3306 EndY=-9.6 EndZ=0
    g246: LineSegment StartX=-24.2648 StartY=-0.4 StartZ=0 EndX=-23.3306 EndY=-0.4 EndZ=0
    g247: LineSegment StartX=-24.2648 StartY=-9.6 StartZ=0 EndX=-24.2648 EndY=-0.4 EndZ=0
    g248: LineSegment StartX=-24.2648 StartY=-0.4 StartZ=0 EndX=-25.2282 EndY=-0.4 EndZ=0
    g249: LineSegment StartX=-24.2648 StartY=-9.6 StartZ=0 EndX=-25.2282 EndY=-9.6 EndZ=0
    g250: LineSegment StartX=-25.2282 StartY=-9.6 StartZ=0 EndX=-25.2282 EndY=-0.4 EndZ=0
    g251: ArcOfEllipse CenterX=-23.5291 CenterY=-12.6066 CenterZ=0 NormalX=0 NormalY=0 NormalZ=1 MajorRadius=2.8 MinorRadius=0.999102 AngleXU=-1.5708 StartAngle=4.34989 EndAngle=4.71239
    g252: ArcOfEllipse CenterX=-23.5291 CenterY=-12.6066 CenterZ=0 NormalX=0 NormalY=0 NormalZ=1 MajorRadius=2.8 MinorRadius=0.999102 AngleXU=-1.5708 StartAngle=4.71239 EndAngle=5.07489
    g253: LineSegment StartX=-23.0159 StartY=0.4 StartZ=0 EndX=-22.0818 EndY=0.4 EndZ=0
    g254: LineSegment StartX=-23.0159 StartY=9.6 StartZ=0 EndX=-22.0818 EndY=9.6 EndZ=0
    g255: LineSegment StartX=-23.0159 StartY=0.4 StartZ=0 EndX=-23.0159 EndY=9.6 EndZ=0
    g256: LineSegment StartX=-23.0159 StartY=0.4 StartZ=0 EndX=-23.9794 EndY=0.4 EndZ=0
    g257: LineSegment StartX=-23.9794 StartY=0.4 StartZ=0 EndX=-23.9794 EndY=9.6 EndZ=0
    g258: LineSegment StartX=-23.0159 StartY=9.6 StartZ=0 EndX=-23.9794 EndY=9.6 EndZ=0
    g259: LineSegment StartX=-23.1879 StartY=-5.4e-15 StartZ=0 EndX=-23.5026 EndY=-5.3e-15 EndZ=0
    g260: LineSegment StartX=-23.5026 StartY=-5.3e-15 StartZ=0 EndX=-23.5026 EndY=0.4 EndZ=0
    g261: LineSegment StartX=-23.5026 StartY=9.6 StartZ=0 EndX=-23.5026 EndY=10 EndZ=0
    g262: LineSegment StartX=-23.1879 StartY=10 StartZ=0 EndX=-23.5026 EndY=10 EndZ=0
    g263: ArcOfEllipse CenterX=-22.3553 CenterY=24.8267 CenterZ=0 NormalX=0 NormalY=0 NormalZ=1 MajorRadius=2.8 MinorRadius=0.999102 AngleXU=-1.5708 StartAngle=4.34989 EndAngle=4.71239
    g264: ArcOfEllipse CenterX=-22.3553 CenterY=24.8267 CenterZ=0 NormalX=0 NormalY=0 NormalZ=1 MajorRadius=2.8 MinorRadius=0.999102 AngleXU=-1.5708 StartAngle=4.71239 EndAngle=5.07489
    g265: ArcOfEllipse CenterX=-23.5291 CenterY=12.6066 CenterZ=0 NormalX=0 NormalY=0 NormalZ=1 MajorRadius=2.8 MinorRadius=0.999102 AngleXU=-1.5708 StartAngle=4.34989 EndAngle=4.71239
    g266: ArcOfEllipse CenterX=-23.5291 CenterY=12.6066 CenterZ=0 NormalX=0 NormalY=0 NormalZ=1 MajorRadius=2.8 MinorRadius=0.999102 AngleXU=-1.5708 StartAngle=4.71239 EndAngle=5.07489
    g267: ArcOfEllipse CenterX=-23.9244 CenterY=-6e-15 CenterZ=0 NormalX=0 NormalY=0 NormalZ=1 MajorRadius=2.8 MinorRadius=0.999102 AngleXU=-1.5708 StartAngle=4.34989 EndAngle=4.71239
    g268: ArcOfEllipse CenterX=-23.9244 CenterY=-6e-15 CenterZ=0 NormalX=0 NormalY=0 NormalZ=1 MajorRadius=2.8 MinorRadius=0.999102 AngleXU=-1.5708 StartAngle=4.71239 EndAngle=4.85574
    g269: LineSegment StartX=-8.24608 StartY=9.51828 StartZ=0 EndX=-8.3323 EndY=9.65903 EndZ=0
    g270: LineSegment StartX=-7.09411 StartY=7.42317 StartZ=0 EndX=-8.24608 EndY=9.51828 EndZ=0
    g271: LineSegment StartX=31.3465 StartY=-4.6e-15 StartZ=0 EndX=31.5162 EndY=-4.6e-15 EndZ=0
    g272: LineSegment StartX=2.28066 StartY=-29.1634 StartZ=0 EndX=1.34649 EndY=-27.5453 EndZ=0
    g273: LineSegment StartX=13.3959 StartY=-23.2024 StartZ=0 EndX=12.4617 EndY=-21.5844 EndZ=0
    g274: LineSegment StartX=-8.88919 StartY=-34.2569 StartZ=0 EndX=-9.82336 EndY=-32.6389 EndZ=0
    g275: LineSegment StartX=24.1159 StartY=-16.5568 StartZ=0 EndX=23.1817 EndY=-14.9387 EndZ=0
    g276: LineSegment StartX=34.112 StartY=-9.4302 StartZ=0 EndX=33.1778 EndY=-7.81217 EndZ=0
    g277: LineSegment StartX=34.112 StartY=9.4302 StartZ=0 EndX=33.1778 EndY=7.81217 EndZ=0
    g278: LineSegment StartX=24.1159 StartY=16.5568 StartZ=0 EndX=23.1817 EndY=14.9387 EndZ=0
    g279: LineSegment StartX=13.3959 StartY=23.2024 StartZ=0 EndX=12.4617 EndY=21.5844 EndZ=0
    g280: LineSegment StartX=2.28066 StartY=29.1634 StartZ=0 EndX=1.34649 EndY=27.5453 EndZ=0
    g281: LineSegment StartX=-8.88919 StartY=34.2569 StartZ=0 EndX=-9.82336 EndY=32.6389 EndZ=0
    g282: LineSegment StartX=-25.2228 StartY=-24.8267 StartZ=0 EndX=-23.3544 EndY=-24.8267 EndZ=0
    g283: LineSegment StartX=-26.3965 StartY=-12.6066 StartZ=0 EndX=-24.5282 EndY=-12.6066 EndZ=0
    g284: LineSegment StartX=-25.2228 StartY=24.8267 StartZ=0 EndX=-23.3544 EndY=24.8267 EndZ=0
    g285: LineSegment StartX=-26.3965 StartY=12.6066 StartZ=0 EndX=-24.5282 EndY=12.6066 EndZ=0
    g286: LineSegment StartX=-26.7918 StartY=-6.3e-15 StartZ=0 EndX=-24.9235 EndY=-6.5e-15 EndZ=0
    g287: LineSegment StartX=-14.9495 StartY=22.2317 StartZ=0 EndX=-14.9495 EndY=22.2317 EndZ=0
    g288: LineSegment StartX=-14.9495 StartY=-22.2317 StartZ=0 EndX=-14.9495 EndY=-22.2317 EndZ=0
    g289: Circle CenterX=-12.3047 CenterY=21.3123 CenterZ=0 NormalX=0 NormalY=0 NormalZ=1 AngleXU=0 Radius=4.2
    g290: Circle CenterX=24.6094 CenterY=0 CenterZ=0 NormalX=0 NormalY=0 NormalZ=1 AngleXU=0 Radius=4.2
    g291: Circle CenterX=-12.3047 CenterY=-21.3123 CenterZ=0 NormalX=0 NormalY=0 NormalZ=1 AngleXU=0 Radius=4.2
    g292: Circle CenterX=0 CenterY=0 CenterZ=0 NormalX=0 NormalY=0 NormalZ=1 AngleXU=0 Radius=4.2
    g293: LineSegment StartX=-12.436 StartY=10 StartZ=0 EndX=-12.436 EndY=3.5 EndZ=0
    g294: LineSegment StartX=-8.93598 StartY=3.5 StartZ=0 EndX=-8.93598 EndY=10 EndZ=0
    g295: ArcOfCircle CenterX=-10.686 CenterY=10 CenterZ=0 NormalX=0 NormalY=0 NormalZ=1 AngleXU=0 Radius=1.75 StartAngle=0 EndAngle=3.14159
    g296: ArcOfCircle CenterX=-10.686 CenterY=3.5 CenterZ=0 NormalX=0 NormalY=0 NormalZ=1 AngleXU=0 Radius=1.75 StartAngle=3.14159 EndAngle=6.28318
    g297: ArcOfCircle CenterX=-3.31726 CenterY=14.2543 CenterZ=0 NormalX=0 NormalY=0 NormalZ=1 AngleXU=0 Radius=1.75 StartAngle=1.0472 EndAngle=4.18879
    g298: ArcOfCircle CenterX=2.31191 CenterY=11.0043 CenterZ=0 NormalX=0 NormalY=0 NormalZ=1 AngleXU=0 Radius=1.75 StartAngle=4.18879 EndAngle=7.33038
    g299: ArcOfCircle CenterX=8.37409 CenterY=7.50434 CenterZ=0 NormalX=0 NormalY=0 NormalZ=1 AngleXU=0 Radius=1.75 StartAngle=1.0472 EndAngle=4.18879
    g300: ArcOfCircle CenterX=14.0033 CenterY=4.25434 CenterZ=0 NormalX=0 NormalY=0 NormalZ=1 AngleXU=0 Radius=1.75 StartAngle=4.18879 EndAngle=7.33038
    g301: ArcOfCircle CenterX=14.0033 CenterY=-4.25434 CenterZ=0 NormalX=0 NormalY=0 NormalZ=1 AngleXU=0 Radius=1.75 StartAngle=5.23599 EndAngle=8.37758
    g302: ArcOfCircle CenterX=8.37409 CenterY=-7.50434 CenterZ=0 NormalX=0 NormalY=0 NormalZ=1 AngleXU=0 Radius=1.75 StartAngle=2.0944 EndAngle=5.23599
    g303: ArcOfCircle CenterX=-10.686 CenterY=-10 CenterZ=0 NormalX=0 NormalY=0 NormalZ=1 AngleXU=0 Radius=1.75 StartAngle=3.14159 EndAngle=6.28319
    g304: ArcOfCircle CenterX=-10.686 CenterY=-3.5 CenterZ=0 NormalX=0 NormalY=0 NormalZ=1 AngleXU=0 Radius=1.75 StartAngle=0 EndAngle=3.14159
    g305: LineSegment StartX=-2.44226 StartY=15.7699 StartZ=0 EndX=3.18691 EndY=12.5199 EndZ=0
    g306: LineSegment StartX=1.43691 StartY=9.48879 StartZ=0 EndX=-4.19226 EndY=12.7388 EndZ=0
    g307: LineSegment StartX=9.24909 StartY=9.01988 StartZ=0 EndX=14.8782 EndY=5.76988 EndZ=0
    g308: LineSegment StartX=13.1283 StartY=2.73879 StartZ=0 EndX=7.49909 EndY=5.98879 EndZ=0
    g309: LineSegment StartX=13.1283 StartY=-2.73879 StartZ=0 EndX=7.49909 EndY=-5.98879 EndZ=0
    g310: LineSegment StartX=14.8782 StartY=-5.76988 StartZ=0 EndX=9.24908 EndY=-9.01988 EndZ=0
    g311: LineSegment StartX=3.18691 StartY=-12.5199 StartZ=0 EndX=-2.44226 EndY=-15.7699 EndZ=0
    g312: LineSegment StartX=-4.19226 StartY=-12.7388 StartZ=0 EndX=1.43691 EndY=-9.48879 EndZ=0
    g313: LineSegment StartX=-12.436 StartY=-10 StartZ=0 EndX=-12.436 EndY=-3.5 EndZ=0
    g314: LineSegment StartX=-8.93598 StartY=-3.5 StartZ=0 EndX=-8.93598 EndY=-10 EndZ=0
    g315: LineSegment StartX=-14.422 StartY=29.3097 StartZ=0 EndX=32.5939 EndY=2.16506 EndZ=0
    g316: LineSegment StartX=32.5939 StartY=-2.16506 StartZ=0 EndX=-14.422 EndY=-29.3097 EndZ=0
    g317: LineSegment StartX=-18.172 StartY=-27.1446 StartZ=0 EndX=-18.172 EndY=27.1446 EndZ=0
    g318: ArcOfCircle CenterX=-15.672 CenterY=27.1446 CenterZ=0 NormalX=0 NormalY=0 NormalZ=1 AngleXU=0 Radius=2.5 StartAngle=1.0472 EndAngle=3.14159
    g319: ArcOfCircle CenterX=31.3439 CenterY=4.3e-15 CenterZ=0 NormalX=0 NormalY=0 NormalZ=1 AngleXU=0 Radius=2.5 StartAngle=5.23599 EndAngle=7.33038
    g320: ArcOfCircle CenterX=-15.672 CenterY=-27.1446 CenterZ=0 NormalX=0 NormalY=0 NormalZ=1 AngleXU=0 Radius=2.5 StartAngle=3.14159 EndAngle=5.23599
    g321: ArcOfCircle CenterX=2.31191 CenterY=-11.0043 CenterZ=0 NormalX=0 NormalY=0 NormalZ=1 AngleXU=0 Radius=1.75 StartAngle=5.23599 EndAngle=8.37758
    g322: ArcOfCircle CenterX=-3.31726 CenterY=-14.2543 CenterZ=0 NormalX=0 NormalY=0 NormalZ=1 AngleXU=0 Radius=1.75 StartAngle=2.0944 EndAngle=5.23599
  constraints (20):
    c: Radius(g292) = 4.2
    c: Equal(g292,g291)
    c: Equal(g291,g290)
    c: Equal(g290,g289)
    c: Coincident(g299,g-7)
    c: Tangent(g315,g318) = 1.5708
    c: Tangent(g317,g318) = 1.5708
    c: Tangent(g316,g319) = 1.5708
    c: Tangent(g315,g319) = 1.5708
    c: Tangent(g316,g320) = 1.5708
    c: Tangent(g317,g320) = 1.5708
    c: PointOnObject(g317,g-26)
    c: PointOnObject(g315,g-25)
    c: PointOnObject(g315,g-25)
    c: PointOnObject(g316,g-27)
    c: PointOnObject(g316,g-27)
    c: PointOnObject(g317,g-26)
    c: Radius(g319) = 2.5
    c: Equal(g320,g319)
    c: Equal(g319,g318)
FEATURE [Sketcher::SketchObject] Sketch001  label="pcb_cuts"
  ExternalGeometry = -> [Shape2DView001]
  FullyConstrained = false
  Placement = pos=(0,0,0) rot=(0,0,1;3.14159rad)
  sketch-geometry (35):
    g0: LineSegment StartX=-14.9495 StartY=22.2317 StartZ=0 EndX=-14.9495 EndY=22.2317 EndZ=0
    g1: Circle CenterX=-12.3047 CenterY=21.3123 CenterZ=0 NormalX=0 NormalY=0 NormalZ=1 AngleXU=0 Radius=4.2
    g2: Circle CenterX=24.6094 CenterY=0 CenterZ=0 NormalX=0 NormalY=0 NormalZ=1 AngleXU=0 Radius=4.2
    g3: Circle CenterX=-12.3047 CenterY=-21.3123 CenterZ=0 NormalX=0 NormalY=0 NormalZ=1 AngleXU=0 Radius=4.2
    g4: Circle CenterX=0 CenterY=0 CenterZ=0 NormalX=0 NormalY=0 NormalZ=1 AngleXU=0 Radius=4.2
    g5: LineSegment StartX=-12.436 StartY=10 StartZ=0 EndX=-12.436 EndY=3.5 EndZ=0
    g6: LineSegment StartX=-8.93598 StartY=3.5 StartZ=0 EndX=-8.93598 EndY=10 EndZ=0
    g7: ArcOfCircle CenterX=-10.686 CenterY=10 CenterZ=0 NormalX=0 NormalY=0 NormalZ=1 AngleXU=0 Radius=1.75 StartAngle=0 EndAngle=3.14159
    g8: ArcOfCircle CenterX=-10.686 CenterY=3.5 CenterZ=0 NormalX=0 NormalY=0 NormalZ=1 AngleXU=0 Radius=1.75 StartAngle=3.14159 EndAngle=6.28318
    g9: ArcOfCircle CenterX=-3.31726 CenterY=14.2543 CenterZ=0 NormalX=0 NormalY=0 NormalZ=1 AngleXU=0 Radius=1.75 StartAngle=1.0472 EndAngle=4.18879
    g10: ArcOfCircle CenterX=2.31191 CenterY=11.0043 CenterZ=0 NormalX=0 NormalY=0 NormalZ=1 AngleXU=0 Radius=1.75 StartAngle=4.18879 EndAngle=7.33038
    g11: ArcOfCircle CenterX=8.37409 CenterY=7.50434 CenterZ=0 NormalX=0 NormalY=0 NormalZ=1 AngleXU=0 Radius=1.75 StartAngle=1.0472 EndAngle=4.18879
    g12: ArcOfCircle CenterX=14.0033 CenterY=4.25434 CenterZ=0 NormalX=0 NormalY=0 NormalZ=1 AngleXU=0 Radius=1.75 StartAngle=4.18879 EndAngle=7.33038
    g13: ArcOfCircle CenterX=14.0033 CenterY=-4.25434 CenterZ=0 NormalX=0 NormalY=0 NormalZ=1 AngleXU=0 Radius=1.75 StartAngle=5.23599 EndAngle=8.37758
    g14: ArcOfCircle CenterX=8.37409 CenterY=-7.50434 CenterZ=0 NormalX=0 NormalY=0 NormalZ=1 AngleXU=0 Radius=1.75 StartAngle=2.0944 EndAngle=5.23599
    g15: ArcOfCircle CenterX=-10.686 CenterY=-10 CenterZ=0 NormalX=0 NormalY=0 NormalZ=1 AngleXU=0 Radius=1.75 StartAngle=3.14159 EndAngle=6.28319
    g16: ArcOfCircle CenterX=-10.686 CenterY=-3.5 CenterZ=0 NormalX=0 NormalY=0 NormalZ=1 AngleXU=0 Radius=1.75 StartAngle=0 EndAngle=3.14159
    g17: LineSegment StartX=-2.44226 StartY=15.7699 StartZ=0 EndX=3.18691 EndY=12.5199 EndZ=0
    g18: LineSegment StartX=1.43691 StartY=9.48879 StartZ=0 EndX=-4.19226 EndY=12.7388 EndZ=0
    g19: LineSegment StartX=9.24909 StartY=9.01988 StartZ=0 EndX=14.8782 EndY=5.76988 EndZ=0
    g20: LineSegment StartX=13.1283 StartY=2.73879 StartZ=0 EndX=7.49909 EndY=5.98879 EndZ=0
    g21: LineSegment StartX=13.1283 StartY=-2.73879 StartZ=0 EndX=7.49909 EndY=-5.98879 EndZ=0
    g22: LineSegment StartX=14.8782 StartY=-5.76988 StartZ=0 EndX=9.24908 EndY=-9.01988 EndZ=0
    g23: LineSegment StartX=3.18691 StartY=-12.5199 StartZ=0 EndX=-2.44226 EndY=-15.7699 EndZ=0
    g24: LineSegment StartX=-4.19226 StartY=-12.7388 StartZ=0 EndX=1.43691 EndY=-9.48879 EndZ=0
    g25: LineSegment StartX=-12.436 StartY=-10 StartZ=0 EndX=-12.436 EndY=-3.5 EndZ=0
    g26: LineSegment StartX=-8.93598 StartY=-3.5 StartZ=0 EndX=-8.93598 EndY=-10 EndZ=0
    g27: LineSegment StartX=-17.422 StartY=32.7738 StartZ=0 EndX=37.0939 EndY=1.29904 EndZ=0
    g28: LineSegment StartX=37.0939 StartY=-1.29904 StartZ=0 EndX=-17.422 EndY=-32.7738 EndZ=0
    g29: LineSegment StartX=-19.672 StartY=-31.4748 StartZ=0 EndX=-19.672 EndY=31.4748 EndZ=0
    g30: ArcOfCircle CenterX=-18.172 CenterY=31.4748 CenterZ=0 NormalX=0 NormalY=0 NormalZ=1 AngleXU=0 Radius=1.5 StartAngle=1.0472 EndAngle=3.14159
    g31: ArcOfCircle CenterX=-18.172 CenterY=-31.4748 CenterZ=0 NormalX=0 NormalY=0 NormalZ=1 AngleXU=0 Radius=1.5 StartAngle=3.14159 EndAngle=5.23599
    g32: ArcOfCircle CenterX=2.31191 CenterY=-11.0043 CenterZ=0 NormalX=0 NormalY=0 NormalZ=1 AngleXU=0 Radius=1.75 StartAngle=5.23599 EndAngle=8.37758
    g33: ArcOfCircle CenterX=-3.31726 CenterY=-14.2543 CenterZ=0 NormalX=0 NormalY=0 NormalZ=1 AngleXU=0 Radius=1.75 StartAngle=2.0944 EndAngle=5.23599
    g34: ArcOfCircle CenterX=36.3439 CenterY=7e-16 CenterZ=0 NormalX=0 NormalY=0 NormalZ=1 AngleXU=0 Radius=1.5 StartAngle=5.23599 EndAngle=7.33038
  constraints (18):
    c: Radius(g4) = 4.2
    c: Equal(g4,g3)
    c: Equal(g3,g2)
    c: Equal(g2,g1)
    c: Coincident(g11,g-7)
    c: Tangent(g27,g30) = 1.5708
    c: Tangent(g29,g30) = 1.5708
    c: Tangent(g28,g31) = 1.5708
    c: Tangent(g29,g31) = 1.5708
    c: Parallel(g-25,g27)
    c: Parallel(g-26,g29)
    c: Parallel(g-27,g28)
    c: Coincident(g30,g-26)
    c: Radius(g30) = 1.5
    c: Coincident(g31,g-27)
    c: Tangent(g27,g34) = 1.5708
    c: Tangent(g28,g34) = 1.5708
    c: Distance(g34,g27) = 1.5
